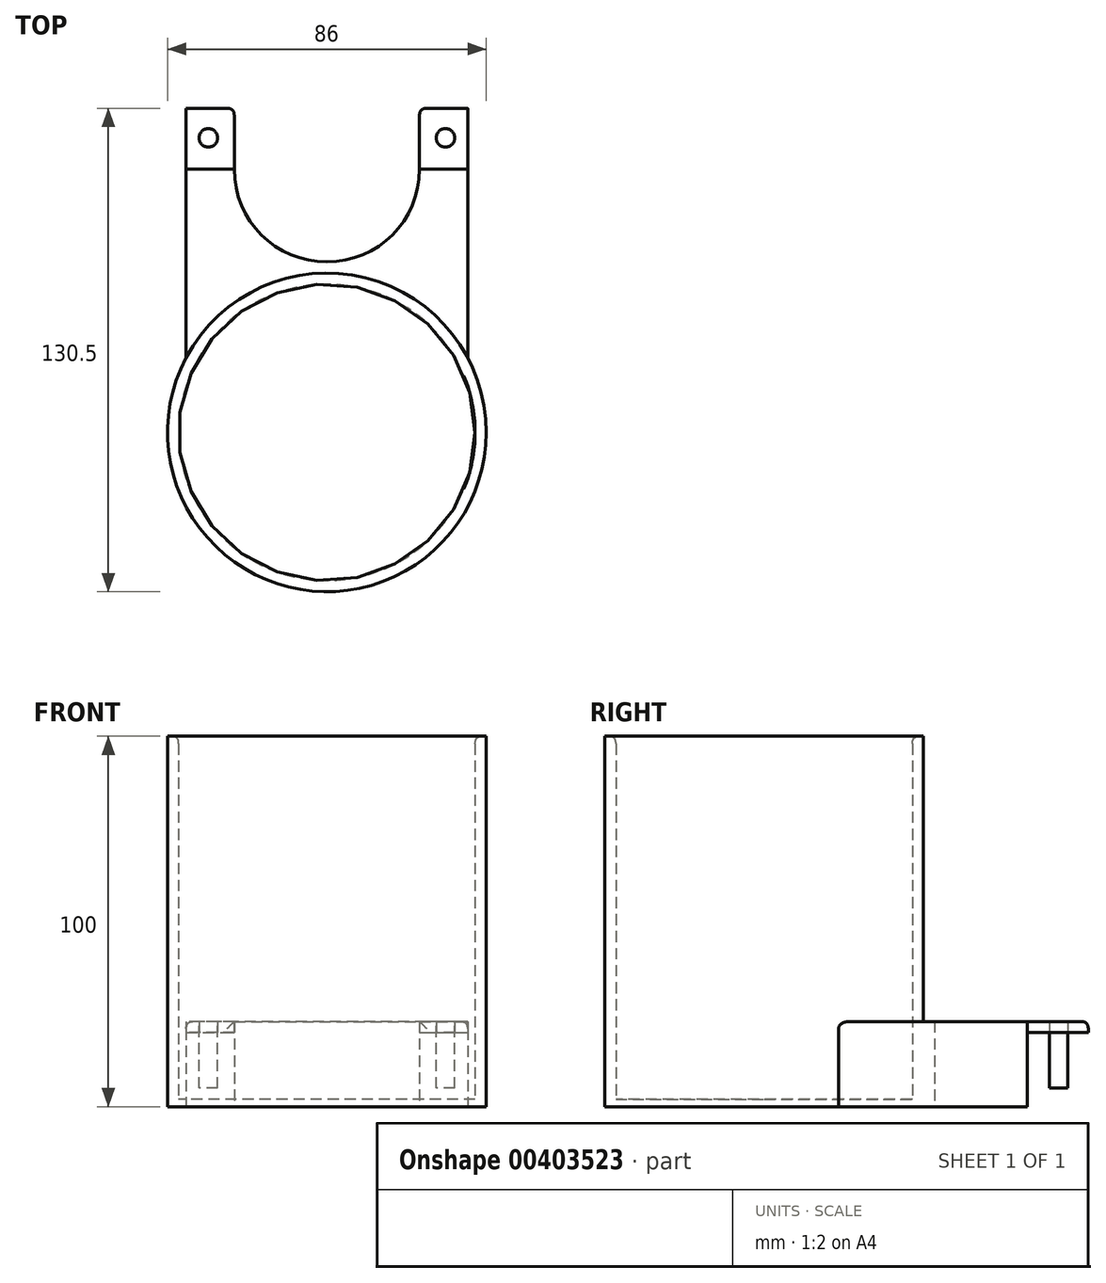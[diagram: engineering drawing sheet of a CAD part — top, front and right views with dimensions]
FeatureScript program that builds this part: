
annotation { "Feature Type Name" : "Feature", "Feature Type Description" : "" }
export const myFeature = defineFeature(function(context is Context, id is Id, definition is map)
    precondition{}
    {
        {
            var Q0;
            Q0=qCreatedBy(makeId("Top.planeOp"),FACE);
            var sketch = newSketch(context, id + "F0", { "sketchPlane" : qUnion([Q0])});
            skPoint(sketch, "E0.middle", {"position": v(0, 0) * mm});
            skLineSegment(sketch, "E1.left", {"start": v(-28, 71) * mm, "end": v(-28, 68) * mm});
            skLineSegment(sketch, "E1.right", {"start": v(28, 71) * mm, "end": v(28, 68) * mm});
            skLineSegment(sketch, "E2.left", {"start": v(28, 71) * mm, "end": v(28, 68.5) * mm});
            skLineSegment(sketch, "E2.right", {"start": v(38, 87.5) * mm, "end": v(38, 68) * mm});
            skLineSegment(sketch, "E3.left", {"start": v(-28, 71) * mm, "end": v(-28, 68.5) * mm});
            skLineSegment(sketch, "E3.right", {"start": v(-38, 87.5) * mm, "end": v(-38, 68) * mm});
            skPoint(sketch, "E4", {"position": v(-32, 79.5) * mm});
            skPoint(sketch, "E5", {"position": v(32, 79.5) * mm});
            skCircle(sketch, "E6", {"center": v(-32, 79.5) * mm, "radius": 2.5 * mm});
            skCircle(sketch, "E7", {"center": v(32, 79.5) * mm, "radius": 2.5 * mm});
            skCircle(sketch, "E8", {"center": v(0, 0) * mm, "radius": 40 * mm});
            skCircle(sketch, "E9", {"center": v(0, 0) * mm, "radius": 43 * mm});
            skPoint(sketch, "E10", {"position": v(0, 71) * mm});
            skArc(sketch, "E11", {"start": v(-28, 71) * mm, "mid": v(0, 43) * mm, "end": v(28, 71) * mm});
            skArc(sketch, "E12", {"start": v(-25, 71) * mm, "mid": v(0, 46) * mm, "end": v(25, 71) * mm});
            skLineSegment(sketch, "E13.top", {"start": v(-38, 32.63) * mm, "end": v(-28, 32.63) * mm});
            skLineSegment(sketch, "E13.left", {"start": v(-38, 68) * mm, "end": v(-38, 32.63) * mm});
            skLineSegment(sketch, "E13.right", {"start": v(-28, 68) * mm, "end": v(-28, 32.63) * mm});
            skLineSegment(sketch, "E14.top", {"start": v(38, 32.63) * mm, "end": v(28, 32.63) * mm});
            skLineSegment(sketch, "E14.left", {"start": v(38, 68) * mm, "end": v(38, 32.63) * mm});
            skLineSegment(sketch, "E14.right", {"start": v(28, 68) * mm, "end": v(28, 32.63) * mm});
            skLineSegment(sketch, "E15", {"start": v(-38, 32.63) * mm, "end": v(-38, 20.12) * mm});
            skLineSegment(sketch, "E16", {"start": v(38, 32.63) * mm, "end": v(38, 20.12) * mm});
            skLineSegment(sketch, "E17", {"start": v(-25, 71) * mm, "end": v(-38, 71) * mm});
            skLineSegment(sketch, "E18", {"start": v(25, 71) * mm, "end": v(38, 71) * mm});
            skLineSegment(sketch, "E19", {"start": v(28, 87.5) * mm, "end": v(38, 87.5) * mm});
            skLineSegment(sketch, "E20", {"start": v(-38, 87.5) * mm, "end": v(-28, 87.5) * mm});
            skLineSegment(sketch, "E21.bottom", {"start": v(-38, 87.5) * mm, "end": v(-25, 87.5) * mm});
            skLineSegment(sketch, "E21.top", {"start": v(-28, 71) * mm, "end": v(-25, 71) * mm});
            skLineSegment(sketch, "E21.left", {"start": v(-38, 87.5) * mm, "end": v(-38, 71) * mm});
            skLineSegment(sketch, "E21.right", {"start": v(-25, 87.5) * mm, "end": v(-25, 71) * mm});
            skLineSegment(sketch, "E22.top", {"start": v(25, 87.5) * mm, "end": v(38, 87.5) * mm});
            skLineSegment(sketch, "E22.left", {"start": v(25, 71) * mm, "end": v(25, 87.5) * mm});
            skLineSegment(sketch, "E22.right", {"start": v(38, 71) * mm, "end": v(38, 87.5) * mm});
            skSolve(sketch);
        }
        {
            var Q0;
            {var subQ5=sQuery(id+"F0.wireOp",EDGE,"E1.left");Q0=makeQuery(id+"F0.imprint","IMPRINT",FACE,{"disambiguationData":[TD([[makeQuery(id+"F0.imprint","IMPRINT",EDGE,{"derivedFrom":subQ5}),-1.0]])]});}
            var Q1;
            {var subQ0=sQuery(id+"F0.wireOp",EDGE,"E13.top");Q1=makeQuery(id+"F0.imprint","IMPRINT",FACE,{"disambiguationData":[TD([[makeQuery(id+"F0.imprint","IMPRINT",EDGE,{"derivedFrom":subQ0}),-1.0]])]});}
            var Q2;
            {var subQ5=sQuery(id+"F0.wireOp",EDGE,"E1.left");Q2=makeQuery(id+"F0.imprint","IMPRINT",FACE,{"disambiguationData":[TD([[makeQuery(id+"F0.imprint","IMPRINT",EDGE,{"derivedFrom":subQ5}),1.0]])]});}
            var Q3;
            {var subQ0=sQuery(id+"F0.wireOp",EDGE,"E12");Q3=makeQuery(id+"F0.imprint","IMPRINT",FACE,{"disambiguationData":[TD([[makeQuery(id+"F0.imprint","IMPRINT",EDGE,{"derivedFrom":subQ0}),-1.0]])]});}
            var Q4;
            {var subQ6=sQuery(id+"F0.wireOp",EDGE,"E1.right");Q4=makeQuery(id+"F0.imprint","IMPRINT",FACE,{"disambiguationData":[TD([[makeQuery(id+"F0.imprint","IMPRINT",EDGE,{"derivedFrom":subQ6}),-1.0]])]});}
            var Q5;
            {var subQ5=sQuery(id+"F0.wireOp",EDGE,"E1.right");Q5=makeQuery(id+"F0.imprint","IMPRINT",FACE,{"disambiguationData":[TD([[makeQuery(id+"F0.imprint","IMPRINT",EDGE,{"derivedFrom":subQ5}),1.0]])]});}
            var Q6;
            {var subQ0=sQuery(id+"F0.wireOp",EDGE,"E14.top");Q6=makeQuery(id+"F0.imprint","IMPRINT",FACE,{"disambiguationData":[TD([[makeQuery(id+"F0.imprint","IMPRINT",EDGE,{"derivedFrom":subQ0}),1.0]])]});}
            extrude(context, id + "F1", {"entities" : qUnion([Q0, Q1, Q2, Q3, Q4, Q5, Q6]), "depth" : 23 * mm});
        }
        {
            var Q0;
            Q0=makeQuery(id+"F0.imprint","IMPRINT",FACE,{"disambiguationData":[TD([[makeQuery(id+"F0.imprint","IMPRINT",EDGE,{"derivedFrom":sQuery(id+"F0.wireOp",EDGE,"E8")}),-1.0]])]});
            extrude(context, id + "F2", {"entities" : qUnion([Q0]), "operationType" : NewBodyOperationType.ADD, "depth" : 100 * mm});
        }
        {
            var Q0;
            Q0=makeQuery(id+"F0.imprint","IMPRINT",FACE,{"disambiguationData":[TD([[makeQuery(id+"F0.imprint","IMPRINT",EDGE,{"derivedFrom":sQuery(id+"F0.wireOp",EDGE,"E8")}),1.0]])]});
            extrude(context, id + "F3", {"entities" : qUnion([Q0]), "operationType" : NewBodyOperationType.ADD, "depth" : 2 * mm});
        }
        {
            var Q0;
            Q0=makeQuery(id+"F0.imprint","IMPRINT",FACE,{"disambiguationData":[TD([[makeQuery(id+"F0.imprint","IMPRINT",EDGE,{"derivedFrom":sQuery(id+"F0.wireOp",EDGE,"E7")}),1.0]])]});
            var Q1;
            Q1=makeQuery(id+"F0.imprint","IMPRINT",FACE,{"disambiguationData":[TD([[makeQuery(id+"F0.imprint","IMPRINT",EDGE,{"derivedFrom":sQuery(id+"F0.wireOp",EDGE,"E6")}),1.0]])]});
            extrude(context, id + "F4", {"entities" : qUnion([Q0, Q1]), "oppositeDirection" : true, "depth" : 18 * mm});
        }
        {
            var Q0;
            Q0=makeQuery(id+"F0.imprint","IMPRINT",FACE,{"disambiguationData":[TD([[makeQuery(id+"F0.imprint","IMPRINT",EDGE,{"derivedFrom":sQuery(id+"F0.wireOp",EDGE,"E7")}),-1.0]])]});
            var Q1;
            Q1=makeQuery(id+"F0.imprint","IMPRINT",FACE,{"disambiguationData":[TD([[makeQuery(id+"F0.imprint","IMPRINT",EDGE,{"derivedFrom":sQuery(id+"F0.wireOp",EDGE,"E6")}),-1.0]])]});
            extrude(context, id + "F5", {"entities" : qUnion([Q0, Q1]), "depth" : 3 * mm});
        }
        {
            var Q0;
            Q0=makeQuery(id+"F5.opExtrude","SWEPT_BODY",BODY,{"disambiguationData":[OSD([sQuery(id+"F0.wireOp",EDGE,"E7"),sQuery(id+"F0.wireOp",EDGE,"E18"),sQuery(id+"F0.wireOp",EDGE,"E22.top"),sQuery(id+"F0.wireOp",EDGE,"E22.left"),sQuery(id+"F0.wireOp",EDGE,"E22.right")])]});
            var Q1;
            Q1=makeQuery(id+"F5.opExtrude","SWEPT_BODY",BODY,{"disambiguationData":[OSD([sQuery(id+"F0.wireOp",EDGE,"E6"),sQuery(id+"F0.wireOp",EDGE,"E17"),sQuery(id+"F0.wireOp",EDGE,"E21.bottom"),sQuery(id+"F0.wireOp",EDGE,"E21.top"),sQuery(id+"F0.wireOp",EDGE,"E21.left"),sQuery(id+"F0.wireOp",EDGE,"E21.right")])]});
            var Q2;
            Q2=qCreatedBy(makeId("Top.planeOp"),FACE);
            transform(context, id + "F6", {"entities" : qUnion([Q0, Q1]), "transformType" : TransformType.TRANSLATION_DISTANCE, "transformDirection" : qUnion([Q2]), "distance" : 20 * mm, "makeCopy" : false});
        }
        {
            var Q0;
            Q0=makeQuery(id+"F4.opExtrude","SWEPT_BODY",BODY,{"disambiguationData":[OSD([sQuery(id+"F0.wireOp",EDGE,"E7")])]});
            var Q1;
            Q1=makeQuery(id+"F4.opExtrude","SWEPT_BODY",BODY,{"disambiguationData":[OSD([sQuery(id+"F0.wireOp",EDGE,"E6")])]});
            var Q2;
            Q2=qCreatedBy(makeId("Top.planeOp"),FACE);
            transform(context, id + "F7", {"entities" : qUnion([Q0, Q1]), "transformType" : TransformType.TRANSLATION_DISTANCE, "transformDirection" : qUnion([Q2]), "distance" : 23 * mm, "makeCopy" : false});
        }
        {
            var Q0;
            Q0=makeQuery(id+"F5.opExtrude","SWEPT_EDGE",EDGE,{"disambiguationData":[OSD([sQuery(id+"F0.wireOp",EDGE,"E22.top"),sQuery(id+"F0.wireOp",EDGE,"E22.right")])]});
            var Q1;
            Q1=makeQuery(id+"F5.opExtrude","SWEPT_EDGE",EDGE,{"disambiguationData":[OSD([sQuery(id+"F0.wireOp",EDGE,"E22.top"),sQuery(id+"F0.wireOp",EDGE,"E22.left")])]});
            var Q2;
            Q2=makeQuery(id+"F5.opExtrude","SWEPT_EDGE",EDGE,{"disambiguationData":[OSD([sQuery(id+"F0.wireOp",EDGE,"E21.bottom"),sQuery(id+"F0.wireOp",EDGE,"E21.right")])]});
            var Q3;
            Q3=makeQuery(id+"F5.opExtrude","SWEPT_EDGE",EDGE,{"disambiguationData":[OSD([sQuery(id+"F0.wireOp",EDGE,"E21.bottom"),sQuery(id+"F0.wireOp",EDGE,"E21.left")])]});
            var Q4;
            Q4=makeQuery(id+"F2.opExtrude","CAP_EDGE",EDGE,{"disambiguationData":[OSD([sQuery(id+"F0.wireOp",EDGE,"E8")])],"isStart":false});
            var Q5;
            Q5=makeQuery(id+"F1.opExtrude","CAP_EDGE",EDGE,{"disambiguationData":[OSD([sQuery(id+"F0.wireOp",EDGE,"E2.right"),sQuery(id+"F0.wireOp",EDGE,"E14.left"),sQuery(id+"F0.wireOp",EDGE,"E16")])],"isStart":false});
            var Q6;
            Q6=makeQuery(id+"F5.opExtrude","CAP_EDGE",EDGE,{"disambiguationData":[OSD([sQuery(id+"F0.wireOp",EDGE,"E22.right")])],"isStart":false});
            var Q7;
            Q7=makeQuery(id+"F5.opExtrude","CAP_EDGE",EDGE,{"disambiguationData":[OSD([sQuery(id+"F0.wireOp",EDGE,"E22.top")])],"isStart":false});
            var Q8;
            Q8=makeQuery(id+"F5.opExtrude","CAP_EDGE",EDGE,{"disambiguationData":[OSD([sQuery(id+"F0.wireOp",EDGE,"E21.bottom")])],"isStart":false});
            var Q9;
            Q9=makeQuery(id+"F1.opExtrude","CAP_EDGE",EDGE,{"disambiguationData":[OSD([sQuery(id+"F0.wireOp",EDGE,"E3.right"),sQuery(id+"F0.wireOp",EDGE,"E13.left"),sQuery(id+"F0.wireOp",EDGE,"E15")])],"isStart":false});
            var Q10;
            Q10=makeQuery(id+"F5.opExtrude","CAP_EDGE",EDGE,{"disambiguationData":[OSD([sQuery(id+"F0.wireOp",EDGE,"E21.left")])],"isStart":false});
            fillet(context, id + "F8", {"entities" : qUnion([Q0, Q1, Q2, Q3, Q4, Q5, Q6, Q7, Q8, Q9, Q10]), "radius" : 2 * mm, "tangentPropagation" : true, "rho" : 0.5, "crossSection" : FilletCrossSection.CONIC, "allowEdgeOverflow" : false});
        }
    });
